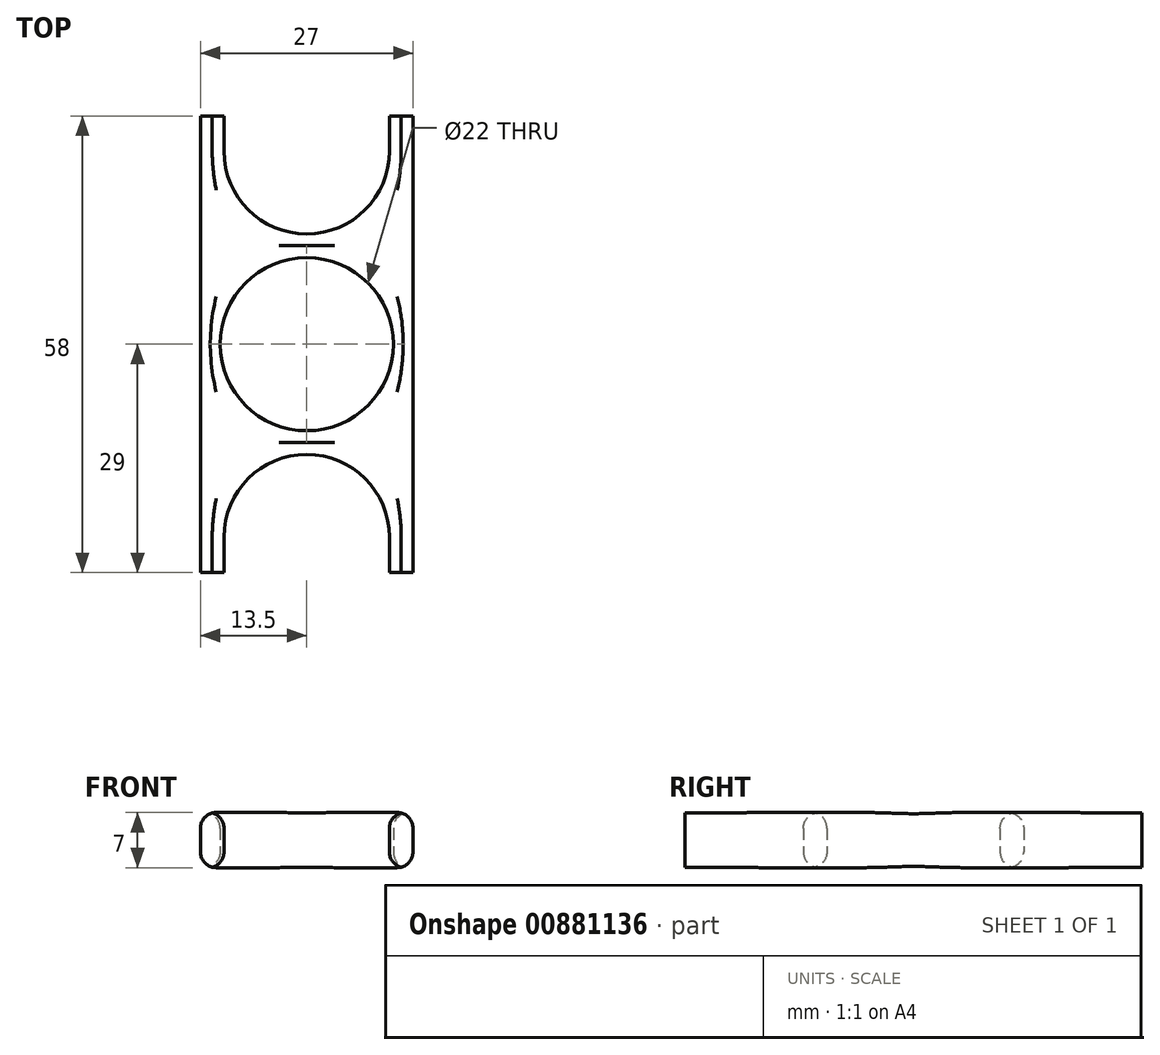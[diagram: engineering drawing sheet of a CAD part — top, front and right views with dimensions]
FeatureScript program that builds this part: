
annotation { "Feature Type Name" : "Feature", "Feature Type Description" : "" }
export const myFeature = defineFeature(function(context is Context, id is Id, definition is map)
    precondition{}
    {
        {
            var Q0;
            Q0=qCreatedBy(makeId("Top.planeOp"),FACE);
            var sketch = newSketch(context, id + "F0", { "sketchPlane" : qUnion([Q0])});
            skLineSegment(sketch, "E0.bottom", {"start": v(13.5, 29) * mm, "end": v(-13.5, 29) * mm});
            skLineSegment(sketch, "E0.top", {"start": v(13.5, -29) * mm, "end": v(-13.5, -29) * mm});
            skLineSegment(sketch, "E0.left", {"start": v(13.5, 29) * mm, "end": v(13.5, -29) * mm});
            skLineSegment(sketch, "E0.right", {"start": v(-13.5, 29) * mm, "end": v(-13.5, -29) * mm});
            skPoint(sketch, "E0.middle", {"position": v(0, 0) * mm});
            skCircle(sketch, "E1", {"center": v(0, 0) * mm, "radius": 11 * mm});
            skLineSegment(sketch, "E2.bottom", {"start": v(10.5, 44) * mm, "end": v(-10.5, 44) * mm});
            skLineSegment(sketch, "E2.top", {"start": v(10.5, 14) * mm, "end": v(-10.5, 14) * mm});
            skLineSegment(sketch, "E2.left", {"start": v(10.5, 44) * mm, "end": v(10.5, 14) * mm});
            skLineSegment(sketch, "E2.right", {"start": v(-10.5, 44) * mm, "end": v(-10.5, 14) * mm});
            skPoint(sketch, "E2.middle", {"position": v(0, 29) * mm});
            skLineSegment(sketch, "E3.bottom", {"start": v(-10.5, -14) * mm, "end": v(10.5, -14) * mm});
            skLineSegment(sketch, "E3.top", {"start": v(-10.5, -44) * mm, "end": v(10.5, -44) * mm});
            skLineSegment(sketch, "E3.left", {"start": v(-10.5, -14) * mm, "end": v(-10.5, -44) * mm});
            skLineSegment(sketch, "E3.right", {"start": v(10.5, -14) * mm, "end": v(10.5, -44) * mm});
            skPoint(sketch, "E3.middle", {"position": v(0, -29) * mm});
            skSolve(sketch);
        }
        {
            var Q0;
            {var subQ5=sQuery(id+"F0.wireOp",EDGE,"E0.left");Q0=makeQuery(id+"F0.imprint","IMPRINT",FACE,{"disambiguationData":[TD([[makeQuery(id+"F0.imprint","IMPRINT",EDGE,{"derivedFrom":subQ5}),-1.0]])]});}
            extrude(context, id + "F1", {"entities" : qUnion([Q0]), "depth" : 7 * mm, "offsetDistance" : 25 * mm});
        }
        {
            var Q0;
            Q0=makeQuery(id+"F1.opExtrude","SWEPT_EDGE",EDGE,{"disambiguationData":[OSD([sQuery(id+"F0.wireOp",EDGE,"E3.bottom"),sQuery(id+"F0.wireOp",EDGE,"E3.left")])]});
            var Q1;
            Q1=makeQuery(id+"F1.opExtrude","SWEPT_EDGE",EDGE,{"disambiguationData":[OSD([sQuery(id+"F0.wireOp",EDGE,"E3.bottom"),sQuery(id+"F0.wireOp",EDGE,"E3.right")])]});
            var Q2;
            Q2=makeQuery(id+"F1.opExtrude","SWEPT_EDGE",EDGE,{"disambiguationData":[OSD([sQuery(id+"F0.wireOp",EDGE,"E2.top"),sQuery(id+"F0.wireOp",EDGE,"E2.right")])]});
            var Q3;
            Q3=makeQuery(id+"F1.opExtrude","SWEPT_EDGE",EDGE,{"disambiguationData":[OSD([sQuery(id+"F0.wireOp",EDGE,"E2.top"),sQuery(id+"F0.wireOp",EDGE,"E2.left")])]});
            fillet(context, id + "F2", {"entities" : qUnion([Q0, Q1, Q2, Q3]), "radius" : 10.5 * mm, "tangentPropagation" : true, "allowEdgeOverflow" : false});
        }
        {
            var Q0;
            Q0=makeQuery(id+"F1.opExtrude","CAP_FACE",FACE,{"disambiguationData":[OSD([sQuery(id+"F0.wireOp",EDGE,"E0.bottom"),sQuery(id+"F0.wireOp",EDGE,"E0.top"),sQuery(id+"F0.wireOp",EDGE,"E0.left"),sQuery(id+"F0.wireOp",EDGE,"E0.right"),sQuery(id+"F0.wireOp",EDGE,"E1"),sQuery(id+"F0.wireOp",EDGE,"E2.top"),sQuery(id+"F0.wireOp",EDGE,"E2.left"),sQuery(id+"F0.wireOp",EDGE,"E2.right"),sQuery(id+"F0.wireOp",EDGE,"E3.bottom"),sQuery(id+"F0.wireOp",EDGE,"E3.left"),sQuery(id+"F0.wireOp",EDGE,"E3.right")])],"isStart":false});
            var Q1;
            Q1=makeQuery(id+"F1.opExtrude","CAP_FACE",FACE,{"disambiguationData":[OSD([sQuery(id+"F0.wireOp",EDGE,"E0.bottom"),sQuery(id+"F0.wireOp",EDGE,"E0.top"),sQuery(id+"F0.wireOp",EDGE,"E0.left"),sQuery(id+"F0.wireOp",EDGE,"E0.right"),sQuery(id+"F0.wireOp",EDGE,"E1"),sQuery(id+"F0.wireOp",EDGE,"E2.top"),sQuery(id+"F0.wireOp",EDGE,"E2.left"),sQuery(id+"F0.wireOp",EDGE,"E2.right"),sQuery(id+"F0.wireOp",EDGE,"E3.bottom"),sQuery(id+"F0.wireOp",EDGE,"E3.left"),sQuery(id+"F0.wireOp",EDGE,"E3.right")])],"isStart":true});
            fillet(context, id + "F3", {"entities" : qUnion([Q0, Q1]), "radius" : 2 * mm, "tangentPropagation" : true, "allowEdgeOverflow" : false});
        }
    });
